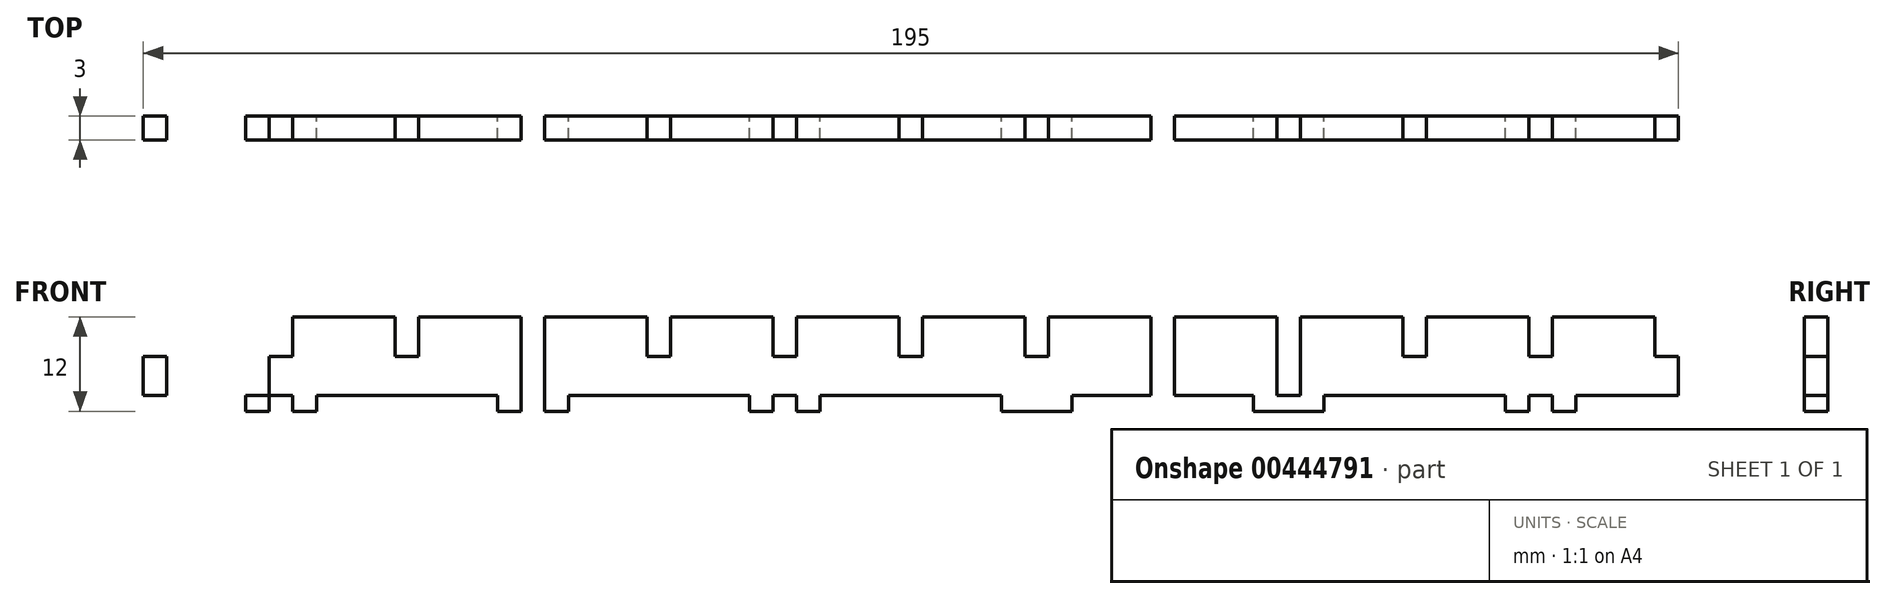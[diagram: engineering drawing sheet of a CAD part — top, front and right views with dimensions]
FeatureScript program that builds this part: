
annotation { "Feature Type Name" : "Feature", "Feature Type Description" : "" }
export const myFeature = defineFeature(function(context is Context, id is Id, definition is map)
    precondition{}
    {
        {
            var Q0;
            Q0=qCreatedBy(makeId("Front.planeOp"),FACE);
            var sketch = newSketch(context, id + "F0", { "sketchPlane" : qUnion([Q0])});
            skLineSegment(sketch, "E0", {"start": v(0, 0) * mm, "end": v(11.5, 0) * mm});
            skLineSegment(sketch, "E1", {"start": v(11.5, 0) * mm, "end": v(11.5, -2) * mm});
            skLineSegment(sketch, "E2", {"start": v(11.5, -2) * mm, "end": v(20.5, -2) * mm});
            skLineSegment(sketch, "E3", {"start": v(20.5, -2) * mm, "end": v(20.5, 0) * mm});
            skLineSegment(sketch, "E4", {"start": v(20.5, 0) * mm, "end": v(43.5, 0) * mm});
            skLineSegment(sketch, "E5", {"start": v(43.5, 0) * mm, "end": v(43.5, -2) * mm});
            skLineSegment(sketch, "E6", {"start": v(43.5, -2) * mm, "end": v(52.5, -2) * mm});
            skLineSegment(sketch, "E7", {"start": v(52.5, -2) * mm, "end": v(52.5, 0) * mm});
            skLineSegment(sketch, "E8", {"start": v(0, 0) * mm, "end": v(0, 10) * mm});
            skPoint(sketch, "E9.oppositeSnap0", {"position": v(0, 5) * mm});
            skLineSegment(sketch, "E9.bottom", {"start": v(0, 10) * mm, "end": v(-1.5, 10) * mm});
            skLineSegment(sketch, "E9.top", {"start": v(0, 5) * mm, "end": v(-1.5, 5) * mm});
            skLineSegment(sketch, "E9.left", {"start": v(0, 10) * mm, "end": v(0, 5) * mm});
            skLineSegment(sketch, "E9.right", {"start": v(-1.5, 10) * mm, "end": v(-1.5, 5) * mm});
            skLineSegment(sketch, "E10.bottom", {"start": v(14.5, 10) * mm, "end": v(17.5, 10) * mm});
            skLineSegment(sketch, "E10.top", {"start": v(14.5, 5) * mm, "end": v(17.5, 5) * mm});
            skLineSegment(sketch, "E10.left", {"start": v(14.5, 10) * mm, "end": v(14.5, 5) * mm});
            skLineSegment(sketch, "E10.right", {"start": v(17.5, 10) * mm, "end": v(17.5, 5) * mm});
            skLineSegment(sketch, "E11.top", {"start": v(0, 0) * mm, "end": v(-1.5, 0) * mm});
            skLineSegment(sketch, "E11.left", {"start": v(0, 5) * mm, "end": v(0, 0) * mm});
            skLineSegment(sketch, "E11.right", {"start": v(-1.5, 5) * mm, "end": v(-1.5, 0) * mm});
            skLineSegment(sketch, "E12.top", {"start": v(14.5, -2) * mm, "end": v(17.5, -2) * mm});
            skLineSegment(sketch, "E12.left", {"start": v(14.5, 5) * mm, "end": v(14.5, -2) * mm});
            skLineSegment(sketch, "E12.right", {"start": v(17.5, 5) * mm, "end": v(17.5, -2) * mm});
            skLineSegment(sketch, "E13.bottom", {"start": v(0, 10) * mm, "end": v(1.5, 10) * mm});
            skLineSegment(sketch, "E13.top", {"start": v(0, 5) * mm, "end": v(1.5, 5) * mm});
            skLineSegment(sketch, "E13.right", {"start": v(1.5, 10) * mm, "end": v(1.5, 5) * mm});
            skLineSegment(sketch, "E14.top", {"start": v(0, 0) * mm, "end": v(1.5, 0) * mm});
            skLineSegment(sketch, "E14.right", {"start": v(1.5, 5) * mm, "end": v(1.5, 0) * mm});
            skLineSegment(sketch, "E15.bottom", {"start": v(11.5, 10) * mm, "end": v(20.5, 10) * mm});
            skLineSegment(sketch, "E15.top", {"start": v(11.5, 13) * mm, "end": v(20.5, 13) * mm});
            skLineSegment(sketch, "E15.left", {"start": v(11.5, 10) * mm, "end": v(11.5, 13) * mm});
            skLineSegment(sketch, "E15.right", {"start": v(20.5, 10) * mm, "end": v(20.5, 13) * mm});
            skLineSegment(sketch, "E16", {"start": v(52.5, 0) * mm, "end": v(75.5, 0) * mm});
            skLineSegment(sketch, "E17", {"start": v(75.5, 0) * mm, "end": v(75.5, -2) * mm});
            skLineSegment(sketch, "E18", {"start": v(75.5, -2) * mm, "end": v(84.5, -2) * mm});
            skLineSegment(sketch, "E19", {"start": v(84.5, -2) * mm, "end": v(84.5, 0) * mm});
            skLineSegment(sketch, "E20", {"start": v(84.5, 0) * mm, "end": v(96, 0) * mm});
            skLineSegment(sketch, "E21", {"start": v(96, 0) * mm, "end": v(96, 19.13) * mm, "construction": true});
            skLineSegment(sketch, "E22", {"start": v(16, 10) * mm, "end": v(16, 11.65) * mm, "construction": true});
            skLineSegment(sketch, "E23.bottom", {"start": v(30.5, 0) * mm, "end": v(33.5, 0) * mm});
            skLineSegment(sketch, "E23.top", {"start": v(30.5, 5) * mm, "end": v(33.5, 5) * mm});
            skLineSegment(sketch, "E23.left", {"start": v(30.5, 0) * mm, "end": v(30.5, 5) * mm});
            skLineSegment(sketch, "E23.right", {"start": v(33.5, 0) * mm, "end": v(33.5, 5) * mm});
            skLineSegment(sketch, "E24.bottom", {"start": v(33.5, 5) * mm, "end": v(30.5, 5) * mm});
            skLineSegment(sketch, "E24.top", {"start": v(33.5, 10) * mm, "end": v(30.5, 10) * mm});
            skLineSegment(sketch, "E24.left", {"start": v(33.5, 5) * mm, "end": v(33.5, 10) * mm});
            skLineSegment(sketch, "E24.right", {"start": v(30.5, 5) * mm, "end": v(30.5, 10) * mm});
            skLineSegment(sketch, "E25", {"start": v(32, 0) * mm, "end": v(32, 2.31) * mm, "construction": true});
            skLineSegment(sketch, "E26.bottom", {"start": v(46.5, -2) * mm, "end": v(49.5, -2) * mm});
            skLineSegment(sketch, "E26.top", {"start": v(46.5, 5) * mm, "end": v(49.5, 5) * mm});
            skLineSegment(sketch, "E26.left", {"start": v(46.5, -2) * mm, "end": v(46.5, 5) * mm});
            skLineSegment(sketch, "E26.right", {"start": v(49.5, -2) * mm, "end": v(49.5, 5) * mm});
            skLineSegment(sketch, "E27.bottom", {"start": v(49.5, 5) * mm, "end": v(46.5, 5) * mm});
            skLineSegment(sketch, "E27.top", {"start": v(49.5, 10) * mm, "end": v(46.5, 10) * mm});
            skLineSegment(sketch, "E27.left", {"start": v(49.5, 5) * mm, "end": v(49.5, 10) * mm});
            skLineSegment(sketch, "E27.right", {"start": v(46.5, 5) * mm, "end": v(46.5, 10) * mm});
            skLineSegment(sketch, "E28.bottom", {"start": v(62.5, 0) * mm, "end": v(65.5, 0) * mm});
            skLineSegment(sketch, "E28.top", {"start": v(62.5, 5) * mm, "end": v(65.5, 5) * mm});
            skLineSegment(sketch, "E28.left", {"start": v(62.5, 0) * mm, "end": v(62.5, 5) * mm});
            skLineSegment(sketch, "E28.right", {"start": v(65.5, 0) * mm, "end": v(65.5, 5) * mm});
            skLineSegment(sketch, "E29.bottom", {"start": v(65.5, 5) * mm, "end": v(62.5, 5) * mm});
            skLineSegment(sketch, "E29.top", {"start": v(65.5, 10) * mm, "end": v(62.5, 10) * mm});
            skLineSegment(sketch, "E29.left", {"start": v(65.5, 5) * mm, "end": v(65.5, 10) * mm});
            skLineSegment(sketch, "E29.right", {"start": v(62.5, 5) * mm, "end": v(62.5, 10) * mm});
            skLineSegment(sketch, "E30.bottom", {"start": v(81.5, -2) * mm, "end": v(78.5, -2) * mm});
            skLineSegment(sketch, "E30.top", {"start": v(81.5, 5) * mm, "end": v(78.5, 5) * mm});
            skLineSegment(sketch, "E30.left", {"start": v(81.5, -2) * mm, "end": v(81.5, 5) * mm});
            skLineSegment(sketch, "E30.right", {"start": v(78.5, -2) * mm, "end": v(78.5, 5) * mm});
            skLineSegment(sketch, "E31.top", {"start": v(81.5, 10) * mm, "end": v(78.5, 10) * mm});
            skLineSegment(sketch, "E31.left", {"start": v(81.5, 5) * mm, "end": v(81.5, 10) * mm});
            skLineSegment(sketch, "E31.right", {"start": v(78.5, 5) * mm, "end": v(78.5, 10) * mm});
            skLineSegment(sketch, "E32.bottom", {"start": v(96, 0) * mm, "end": v(94.5, 0) * mm});
            skLineSegment(sketch, "E32.top", {"start": v(96, 5) * mm, "end": v(94.5, 5) * mm});
            skLineSegment(sketch, "E32.left", {"start": v(96, 0) * mm, "end": v(96, 5) * mm});
            skLineSegment(sketch, "E32.right", {"start": v(94.5, 0) * mm, "end": v(94.5, 5) * mm});
            skLineSegment(sketch, "E33.left", {"start": v(96, 5) * mm, "end": v(96, 5) * mm});
            skLineSegment(sketch, "E33.right", {"start": v(94.5, 5) * mm, "end": v(94.5, 5) * mm});
            skLineSegment(sketch, "E34.top", {"start": v(96, 10) * mm, "end": v(94.5, 10) * mm});
            skLineSegment(sketch, "E34.left", {"start": v(96, 5) * mm, "end": v(96, 10) * mm});
            skLineSegment(sketch, "E34.right", {"start": v(94.5, 5) * mm, "end": v(94.5, 10) * mm});
            skLineSegment(sketch, "E35", {"start": v(48, -2) * mm, "end": v(48, 0) * mm, "construction": true});
            skLineSegment(sketch, "E36", {"start": v(64, 0) * mm, "end": v(64, 2.67) * mm, "construction": true});
            skLineSegment(sketch, "E37", {"start": v(80, -2) * mm, "end": v(80, 0) * mm, "construction": true});
            skLineSegment(sketch, "E38", {"start": v(1.5, 10) * mm, "end": v(96, 10) * mm});
            skLineSegment(sketch, "E39.MirrorCS", {"start": v(96, 5) * mm, "end": v(97.5, 5) * mm});
            skLineSegment(sketch, "E40.MirrorCS", {"start": v(145.5, 5) * mm, "end": v(142.5, 5) * mm});
            skLineSegment(sketch, "E41.MirrorCS", {"start": v(110.5, 5) * mm, "end": v(113.5, 5) * mm});
            skLineSegment(sketch, "E42.MirrorCS", {"start": v(129.5, 5) * mm, "end": v(126.5, 5) * mm});
            skLineSegment(sketch, "E43.MirrorCS", {"start": v(177.5, 5) * mm, "end": v(174.5, 5) * mm});
            skLineSegment(sketch, "E44.MirrorCS", {"start": v(192, 5) * mm, "end": v(190.5, 5) * mm});
            skLineSegment(sketch, "E45.MirrorCS", {"start": v(192, 5) * mm, "end": v(193.5, 5) * mm});
            skLineSegment(sketch, "E46.MirrorCS", {"start": v(142.5, 5) * mm, "end": v(145.5, 5) * mm});
            skLineSegment(sketch, "E47.MirrorCS", {"start": v(126.5, 5) * mm, "end": v(129.5, 5) * mm});
            skLineSegment(sketch, "E48.MirrorCS", {"start": v(192, 10) * mm, "end": v(190.5, 10) * mm});
            skLineSegment(sketch, "E49.MirrorCS", {"start": v(171.5, -2) * mm, "end": v(171.5, 0) * mm});
            skLineSegment(sketch, "E50.MirrorCS", {"start": v(180.5, 0) * mm, "end": v(180.5, -2) * mm});
            skLineSegment(sketch, "E51.MirrorCS", {"start": v(177.5, 10) * mm, "end": v(174.5, 10) * mm});
            skLineSegment(sketch, "E52.MirrorCS", {"start": v(116.5, 0) * mm, "end": v(116.5, -2) * mm});
            skLineSegment(sketch, "E53.MirrorCS", {"start": v(177.5, -2) * mm, "end": v(174.5, -2) * mm});
            skLineSegment(sketch, "E54.MirrorCS", {"start": v(192, 0) * mm, "end": v(190.5, 0) * mm});
            skLineSegment(sketch, "E55.MirrorCS", {"start": v(126.5, 10) * mm, "end": v(129.5, 10) * mm});
            skLineSegment(sketch, "E56.MirrorCS", {"start": v(145.5, -2) * mm, "end": v(142.5, -2) * mm});
            skLineSegment(sketch, "E57.MirrorCS", {"start": v(110.5, -2) * mm, "end": v(113.5, -2) * mm});
            skLineSegment(sketch, "E58.MirrorCS", {"start": v(192, 0) * mm, "end": v(193.5, 0) * mm});
            skLineSegment(sketch, "E59.MirrorCS", {"start": v(96, 10) * mm, "end": v(97.5, 10) * mm});
            skLineSegment(sketch, "E60.MirrorCS", {"start": v(110.5, 10) * mm, "end": v(113.5, 10) * mm});
            skLineSegment(sketch, "E61.MirrorCS", {"start": v(142.5, 10) * mm, "end": v(145.5, 10) * mm});
            skLineSegment(sketch, "E62.MirrorCS", {"start": v(107.5, -2) * mm, "end": v(107.5, 0) * mm});
            skLineSegment(sketch, "E63.MirrorCS", {"start": v(192, 10) * mm, "end": v(193.5, 10) * mm});
            skLineSegment(sketch, "E64.MirrorCS", {"start": v(96, 0) * mm, "end": v(97.5, 0) * mm});
            skLineSegment(sketch, "E65.MirrorCS", {"start": v(139.5, -2) * mm, "end": v(139.5, 0) * mm});
            skLineSegment(sketch, "E66.MirrorCS", {"start": v(129.5, 0) * mm, "end": v(126.5, 0) * mm});
            skLineSegment(sketch, "E67.MirrorCS", {"start": v(148.5, 0) * mm, "end": v(148.5, -2) * mm});
            skLineSegment(sketch, "E68.MirrorCS", {"start": v(192, 5) * mm, "end": v(192, 0) * mm});
            skLineSegment(sketch, "E69.MirrorCS", {"start": v(112, -2) * mm, "end": v(112, 0) * mm, "construction": true});
            skLineSegment(sketch, "E70.MirrorCS", {"start": v(176, 10) * mm, "end": v(176, 11.65) * mm, "construction": true});
            skLineSegment(sketch, "E71.MirrorCS", {"start": v(192, 10) * mm, "end": v(192, 5) * mm});
            skLineSegment(sketch, "E72.MirrorCS", {"start": v(161.5, 0) * mm, "end": v(158.5, 0) * mm});
            skLineSegment(sketch, "E73.MirrorCS", {"start": v(128, 0) * mm, "end": v(128, 2.67) * mm, "construction": true});
            skLineSegment(sketch, "E74.MirrorCS", {"start": v(160, 0) * mm, "end": v(160, 2.31) * mm, "construction": true});
            skLineSegment(sketch, "E75.MirrorCS", {"start": v(144, -2) * mm, "end": v(144, 0) * mm, "construction": true});
            skLineSegment(sketch, "E76.MirrorCS", {"start": v(161.5, 5) * mm, "end": v(158.5, 5) * mm});
            skLineSegment(sketch, "E77.MirrorCS", {"start": v(171.5, 0) * mm, "end": v(148.5, 0) * mm});
            skLineSegment(sketch, "E78.MirrorCS", {"start": v(180.5, -2) * mm, "end": v(171.5, -2) * mm});
            skLineSegment(sketch, "E79.MirrorCS", {"start": v(192, 0) * mm, "end": v(180.5, 0) * mm});
            skLineSegment(sketch, "E80.MirrorCS", {"start": v(177.5, 10) * mm, "end": v(177.5, 5) * mm});
            skLineSegment(sketch, "E81.MirrorCS", {"start": v(158.5, 0) * mm, "end": v(158.5, 5) * mm});
            skLineSegment(sketch, "E82.MirrorCS", {"start": v(129.5, 0) * mm, "end": v(129.5, 5) * mm});
            skLineSegment(sketch, "E83.MirrorCS", {"start": v(97.5, 5) * mm, "end": v(97.5, 10) * mm});
            skPoint(sketch, "E84.MirrorP", {"position": v(192, 5) * mm});
            skLineSegment(sketch, "E85.MirrorCS", {"start": v(139.5, 0) * mm, "end": v(116.5, 0) * mm});
            skLineSegment(sketch, "E86.MirrorCS", {"start": v(126.5, 5) * mm, "end": v(126.5, 10) * mm});
            skLineSegment(sketch, "E87.MirrorCS", {"start": v(161.5, 5) * mm, "end": v(161.5, 10) * mm});
            skLineSegment(sketch, "E88.MirrorCS", {"start": v(180.5, 10) * mm, "end": v(180.5, 13) * mm});
            skLineSegment(sketch, "E89.MirrorCS", {"start": v(180.5, 13) * mm, "end": v(171.5, 13) * mm});
            skLineSegment(sketch, "E90.MirrorCS", {"start": v(158.5, 5) * mm, "end": v(158.5, 10) * mm});
            skLineSegment(sketch, "E91.MirrorCS", {"start": v(161.5, 0) * mm, "end": v(161.5, 5) * mm});
            skLineSegment(sketch, "E92.MirrorCS", {"start": v(107.5, 0) * mm, "end": v(96, 0) * mm});
            skLineSegment(sketch, "E93.MirrorCS", {"start": v(142.5, 5) * mm, "end": v(142.5, 10) * mm});
            skLineSegment(sketch, "E94.MirrorCS", {"start": v(193.5, 5) * mm, "end": v(193.5, 0) * mm});
            skLineSegment(sketch, "E95.MirrorCS", {"start": v(110.5, 5) * mm, "end": v(110.5, 10) * mm});
            skLineSegment(sketch, "E96.MirrorCS", {"start": v(180.5, 10) * mm, "end": v(171.5, 10) * mm});
            skLineSegment(sketch, "E97.MirrorCS", {"start": v(158.5, 10) * mm, "end": v(161.5, 10) * mm});
            skLineSegment(sketch, "E98.MirrorCS", {"start": v(145.5, 5) * mm, "end": v(145.5, 10) * mm});
            skLineSegment(sketch, "E99.MirrorCS", {"start": v(113.5, -2) * mm, "end": v(113.5, 5) * mm});
            skLineSegment(sketch, "E100.MirrorCS", {"start": v(174.5, 5) * mm, "end": v(174.5, -2) * mm});
            skLineSegment(sketch, "E101.MirrorCS", {"start": v(142.5, -2) * mm, "end": v(142.5, 5) * mm});
            skLineSegment(sketch, "E102.MirrorCS", {"start": v(113.5, 5) * mm, "end": v(113.5, 10) * mm});
            skLineSegment(sketch, "E103.MirrorCS", {"start": v(190.5, 10) * mm, "end": v(96, 10) * mm});
            skLineSegment(sketch, "E104.MirrorCS", {"start": v(190.5, 5) * mm, "end": v(190.5, 0) * mm});
            skLineSegment(sketch, "E105.MirrorCS", {"start": v(158.5, 5) * mm, "end": v(161.5, 5) * mm});
            skLineSegment(sketch, "E106.MirrorCS", {"start": v(126.5, 0) * mm, "end": v(126.5, 5) * mm});
            skLineSegment(sketch, "E107.MirrorCS", {"start": v(97.5, 0) * mm, "end": v(97.5, 5) * mm});
            skLineSegment(sketch, "E108.MirrorCS", {"start": v(174.5, 10) * mm, "end": v(174.5, 5) * mm});
            skLineSegment(sketch, "E109.MirrorCS", {"start": v(110.5, -2) * mm, "end": v(110.5, 5) * mm});
            skLineSegment(sketch, "E110.MirrorCS", {"start": v(177.5, 5) * mm, "end": v(177.5, -2) * mm});
            skLineSegment(sketch, "E111.MirrorCS", {"start": v(116.5, -2) * mm, "end": v(107.5, -2) * mm});
            skLineSegment(sketch, "E112.MirrorCS", {"start": v(145.5, -2) * mm, "end": v(145.5, 5) * mm});
            skLineSegment(sketch, "E113.MirrorCS", {"start": v(193.5, 10) * mm, "end": v(193.5, 5) * mm});
            skLineSegment(sketch, "E114.MirrorCS", {"start": v(129.5, 5) * mm, "end": v(129.5, 10) * mm});
            skLineSegment(sketch, "E115.MirrorCS", {"start": v(192, 0) * mm, "end": v(192, 10) * mm});
            skLineSegment(sketch, "E116.MirrorCS", {"start": v(148.5, -2) * mm, "end": v(139.5, -2) * mm});
            skLineSegment(sketch, "E117.MirrorCS", {"start": v(171.5, 10) * mm, "end": v(171.5, 13) * mm});
            skLineSegment(sketch, "E118.MirrorCS", {"start": v(190.5, 10) * mm, "end": v(190.5, 5) * mm});
            skLineSegment(sketch, "E119.top", {"start": v(14.5, 13) * mm, "end": v(17.5, 13) * mm});
            skLineSegment(sketch, "E119.left", {"start": v(14.5, 10) * mm, "end": v(14.5, 13) * mm});
            skLineSegment(sketch, "E119.right", {"start": v(17.5, 10) * mm, "end": v(17.5, 13) * mm});
            skLineSegment(sketch, "E120.bottom", {"start": v(174.5, 10) * mm, "end": v(177.5, 10) * mm});
            skLineSegment(sketch, "E120.top", {"start": v(174.5, 13) * mm, "end": v(177.5, 13) * mm});
            skLineSegment(sketch, "E120.left", {"start": v(174.5, 10) * mm, "end": v(174.5, 13) * mm});
            skLineSegment(sketch, "E120.right", {"start": v(177.5, 10) * mm, "end": v(177.5, 13) * mm});
            skLineSegment(sketch, "E121", {"start": v(11.5, 0) * mm, "end": v(180.5, 0) * mm});
            skSolve(sketch);
        }
        {
            var Q0;
            {var subQ5=sQuery(id+"F0.wireOp",EDGE,"E0");Q0=makeQuery(id+"F0.imprint","IMPRINT",FACE,{"disambiguationData":[TD([[makeQuery(id+"F0.imprint","IMPRINT",EDGE,{"derivedFrom":subQ5}),1.0]])]});}
            var Q1;
            {var subQ2=sQuery(id+"F0.wireOp",EDGE,"E10.right");Q1=makeQuery(id+"F0.imprint","IMPRINT",FACE,{"disambiguationData":[TD([[makeQuery(id+"F0.imprint","IMPRINT",EDGE,{"derivedFrom":subQ2}),1.0]])]});}
            var Q2;
            {var subQ0=sQuery(id+"F0.wireOp",EDGE,"E5");Q2=makeQuery(id+"F0.imprint","IMPRINT",FACE,{"disambiguationData":[TD([[makeQuery(id+"F0.imprint","IMPRINT",EDGE,{"derivedFrom":subQ0}),1.0]])]});}
            var Q3;
            {var subQ0=sQuery(id+"F0.wireOp",EDGE,"E7");Q3=makeQuery(id+"F0.imprint","IMPRINT",FACE,{"disambiguationData":[TD([[makeQuery(id+"F0.imprint","IMPRINT",EDGE,{"derivedFrom":subQ0}),1.0]])]});}
            var Q4;
            {var subQ0=sQuery(id+"F0.wireOp",EDGE,"E17");Q4=makeQuery(id+"F0.imprint","IMPRINT",FACE,{"disambiguationData":[TD([[makeQuery(id+"F0.imprint","IMPRINT",EDGE,{"derivedFrom":subQ0}),1.0]])]});}
            var Q5;
            {var subQ0=sQuery(id+"F0.wireOp",EDGE,"E19");Q5=makeQuery(id+"F0.imprint","IMPRINT",FACE,{"disambiguationData":[TD([[makeQuery(id+"F0.imprint","IMPRINT",EDGE,{"derivedFrom":subQ0}),1.0]])]});}
            var Q6;
            {var subQ0=sQuery(id+"F0.wireOp",EDGE,"E62.MirrorCS");Q6=makeQuery(id+"F0.imprint","IMPRINT",FACE,{"disambiguationData":[TD([[makeQuery(id+"F0.imprint","IMPRINT",EDGE,{"derivedFrom":subQ0}),-1.0]])]});}
            var Q7;
            {var subQ0=sQuery(id+"F0.wireOp",EDGE,"E52.MirrorCS");Q7=makeQuery(id+"F0.imprint","IMPRINT",FACE,{"disambiguationData":[TD([[makeQuery(id+"F0.imprint","IMPRINT",EDGE,{"derivedFrom":subQ0}),-1.0]])]});}
            var Q8;
            {var subQ0=sQuery(id+"F0.wireOp",EDGE,"E65.MirrorCS");Q8=makeQuery(id+"F0.imprint","IMPRINT",FACE,{"disambiguationData":[TD([[makeQuery(id+"F0.imprint","IMPRINT",EDGE,{"derivedFrom":subQ0}),-1.0]])]});}
            var Q9;
            {var subQ0=sQuery(id+"F0.wireOp",EDGE,"E67.MirrorCS");Q9=makeQuery(id+"F0.imprint","IMPRINT",FACE,{"disambiguationData":[TD([[makeQuery(id+"F0.imprint","IMPRINT",EDGE,{"derivedFrom":subQ0}),-1.0]])]});}
            var Q10;
            {var subQ0=sQuery(id+"F0.wireOp",EDGE,"E49.MirrorCS");Q10=makeQuery(id+"F0.imprint","IMPRINT",FACE,{"disambiguationData":[TD([[makeQuery(id+"F0.imprint","IMPRINT",EDGE,{"derivedFrom":subQ0}),-1.0]])]});}
            var Q11;
            {var subQ0=sQuery(id+"F0.wireOp",EDGE,"E50.MirrorCS");Q11=makeQuery(id+"F0.imprint","IMPRINT",FACE,{"disambiguationData":[TD([[makeQuery(id+"F0.imprint","IMPRINT",EDGE,{"derivedFrom":subQ0}),-1.0]])]});}
            var Q12;
            {var subQ1=sQuery(id+"F0.wireOp",EDGE,"E23.right");Q12=makeQuery(id+"F0.imprint","IMPRINT",FACE,{"disambiguationData":[TD([[makeQuery(id+"F0.imprint","IMPRINT",EDGE,{"derivedFrom":subQ1}),-1.0]])]});}
            var Q13;
            {var subQ2=sQuery(id+"F0.wireOp",EDGE,"E27.left");Q13=makeQuery(id+"F0.imprint","IMPRINT",FACE,{"disambiguationData":[TD([[makeQuery(id+"F0.imprint","IMPRINT",EDGE,{"derivedFrom":subQ2}),-1.0]])]});}
            var Q14;
            {var subQ1=sQuery(id+"F0.wireOp",EDGE,"E28.right");Q14=makeQuery(id+"F0.imprint","IMPRINT",FACE,{"disambiguationData":[TD([[makeQuery(id+"F0.imprint","IMPRINT",EDGE,{"derivedFrom":subQ1}),-1.0]])]});}
            var Q15;
            {var subQ2=sQuery(id+"F0.wireOp",EDGE,"E31.left");Q15=makeQuery(id+"F0.imprint","IMPRINT",FACE,{"disambiguationData":[TD([[makeQuery(id+"F0.imprint","IMPRINT",EDGE,{"derivedFrom":subQ2}),-1.0]])]});}
            var Q16;
            {var subQ2=sQuery(id+"F0.wireOp",EDGE,"E83.MirrorCS");Q16=makeQuery(id+"F0.imprint","IMPRINT",FACE,{"disambiguationData":[TD([[makeQuery(id+"F0.imprint","IMPRINT",EDGE,{"derivedFrom":subQ2}),-1.0]])]});}
            var Q17;
            {var subQ1=sQuery(id+"F0.wireOp",EDGE,"E86.MirrorCS");Q17=makeQuery(id+"F0.imprint","IMPRINT",FACE,{"disambiguationData":[TD([[makeQuery(id+"F0.imprint","IMPRINT",EDGE,{"derivedFrom":subQ1}),1.0]])]});}
            var Q18;
            {var subQ6=sQuery(id+"F0.wireOp",EDGE,"E82.MirrorCS");Q18=makeQuery(id+"F0.imprint","IMPRINT",FACE,{"disambiguationData":[TD([[makeQuery(id+"F0.imprint","IMPRINT",EDGE,{"derivedFrom":subQ6}),-1.0]])]});}
            var Q19;
            {var subQ7=sQuery(id+"F0.wireOp",EDGE,"E81.MirrorCS");Q19=makeQuery(id+"F0.imprint","IMPRINT",FACE,{"disambiguationData":[TD([[makeQuery(id+"F0.imprint","IMPRINT",EDGE,{"derivedFrom":subQ7}),1.0]])]});}
            var Q20;
            {var subQ7=sQuery(id+"F0.wireOp",EDGE,"E87.MirrorCS");Q20=makeQuery(id+"F0.imprint","IMPRINT",FACE,{"disambiguationData":[TD([[makeQuery(id+"F0.imprint","IMPRINT",EDGE,{"derivedFrom":subQ7}),-1.0]])]});}
            var Q21;
            {var subQ1=sQuery(id+"F0.wireOp",EDGE,"E80.MirrorCS");Q21=makeQuery(id+"F0.imprint","IMPRINT",FACE,{"disambiguationData":[TD([[makeQuery(id+"F0.imprint","IMPRINT",EDGE,{"derivedFrom":subQ1}),1.0]])]});}
            var Q22;
            Q22=makeQuery(id+"F0.imprint","IMPRINT",FACE,{"disambiguationData":[TD([[makeQuery(id+"F0.imprint","IMPRINT",EDGE,{"derivedFrom":sQuery(id+"F0.wireOp",EDGE,"E13.top")}),-1.0]])]});
            var Q23;
            Q23=makeQuery(id+"F0.imprint","IMPRINT",FACE,{"disambiguationData":[TD([[makeQuery(id+"F0.imprint","IMPRINT",EDGE,{"derivedFrom":sQuery(id+"F0.wireOp",EDGE,"E9.top")}),1.0]])]});
            var Q24;
            {var subQ0=sQuery(id+"F0.wireOp",EDGE,"E12.top");Q24=makeQuery(id+"F0.imprint","IMPRINT",FACE,{"disambiguationData":[TD([[makeQuery(id+"F0.imprint","IMPRINT",EDGE,{"derivedFrom":subQ0}),1.0]])]});}
            var Q25;
            {var subQ0=sQuery(id+"F0.wireOp",EDGE,"E10.top");Q25=makeQuery(id+"F0.imprint","IMPRINT",FACE,{"disambiguationData":[TD([[makeQuery(id+"F0.imprint","IMPRINT",EDGE,{"derivedFrom":subQ0}),-1.0]])]});}
            var Q26;
            {var subQ0=sQuery(id+"F0.wireOp",EDGE,"E23.left");Q26=makeQuery(id+"F0.imprint","IMPRINT",FACE,{"disambiguationData":[TD([[makeQuery(id+"F0.imprint","IMPRINT",EDGE,{"derivedFrom":subQ0}),-1.0]])]});}
            var Q27;
            {var subQ0=sQuery(id+"F0.wireOp",EDGE,"E26.bottom");Q27=makeQuery(id+"F0.imprint","IMPRINT",FACE,{"disambiguationData":[TD([[makeQuery(id+"F0.imprint","IMPRINT",EDGE,{"derivedFrom":subQ0}),1.0]])]});}
            var Q28;
            {var subQ0=sQuery(id+"F0.wireOp",EDGE,"E27.bottom");Q28=makeQuery(id+"F0.imprint","IMPRINT",FACE,{"disambiguationData":[TD([[makeQuery(id+"F0.imprint","IMPRINT",EDGE,{"derivedFrom":subQ0}),1.0]])]});}
            var Q29;
            {var subQ0=sQuery(id+"F0.wireOp",EDGE,"E1");Q29=makeQuery(id+"F0.imprint","IMPRINT",FACE,{"disambiguationData":[TD([[makeQuery(id+"F0.imprint","IMPRINT",EDGE,{"derivedFrom":subQ0}),1.0]])]});}
            var Q30;
            {var subQ0=sQuery(id+"F0.wireOp",EDGE,"E3");Q30=makeQuery(id+"F0.imprint","IMPRINT",FACE,{"disambiguationData":[TD([[makeQuery(id+"F0.imprint","IMPRINT",EDGE,{"derivedFrom":subQ0}),1.0]])]});}
            var Q31;
            {var subQ0=sQuery(id+"F0.wireOp",EDGE,"E28.left");Q31=makeQuery(id+"F0.imprint","IMPRINT",FACE,{"disambiguationData":[TD([[makeQuery(id+"F0.imprint","IMPRINT",EDGE,{"derivedFrom":subQ0}),-1.0]])]});}
            var Q32;
            {var subQ0=sQuery(id+"F0.wireOp",EDGE,"E30.top");Q32=makeQuery(id+"F0.imprint","IMPRINT",FACE,{"disambiguationData":[TD([[makeQuery(id+"F0.imprint","IMPRINT",EDGE,{"derivedFrom":subQ0}),1.0]])]});}
            var Q33;
            {var subQ0=sQuery(id+"F0.wireOp",EDGE,"E30.bottom");Q33=makeQuery(id+"F0.imprint","IMPRINT",FACE,{"disambiguationData":[TD([[makeQuery(id+"F0.imprint","IMPRINT",EDGE,{"derivedFrom":subQ0}),-1.0]])]});}
            var Q34;
            Q34=makeQuery(id+"F0.imprint","IMPRINT",FACE,{"disambiguationData":[TD([[makeQuery(id+"F0.imprint","IMPRINT",EDGE,{"derivedFrom":sQuery(id+"F0.wireOp",EDGE,"E39.MirrorCS")}),-1.0]])]});
            var Q35;
            {var subQ0=sQuery(id+"F0.wireOp",EDGE,"E41.MirrorCS");Q35=makeQuery(id+"F0.imprint","IMPRINT",FACE,{"disambiguationData":[TD([[makeQuery(id+"F0.imprint","IMPRINT",EDGE,{"derivedFrom":subQ0}),-1.0]])]});}
            var Q36;
            {var subQ0=sQuery(id+"F0.wireOp",EDGE,"E111.MirrorCS");var subQ1=sQuery(id+"F0.wireOp",EDGE,"E99.MirrorCS");var subQ2=makeQuery(id+"F0.imprint","INTERSECT",VERTEX,{"derivedFrom":[subQ1,subQ0]});Q36=makeQuery(id+"F0.imprint","IMPRINT",FACE,{"disambiguationData":[TD([[makeQuery(id+"F0.imprint","IMPRINT",EDGE,{"disambiguationData":[TD([[subQ2,-1.0]])],"derivedFrom":subQ1}),1.0]])]});}
            var Q37;
            Q37=makeQuery(id+"F0.imprint","IMPRINT",FACE,{"disambiguationData":[TD([[makeQuery(id+"F0.imprint","IMPRINT",EDGE,{"derivedFrom":sQuery(id+"F0.wireOp",EDGE,"E47.MirrorCS")}),-1.0]])]});
            var Q38;
            {var subQ0=sQuery(id+"F0.wireOp",EDGE,"E46.MirrorCS");Q38=makeQuery(id+"F0.imprint","IMPRINT",FACE,{"disambiguationData":[TD([[makeQuery(id+"F0.imprint","IMPRINT",EDGE,{"derivedFrom":subQ0}),-1.0]])]});}
            var Q39;
            {var subQ0=sQuery(id+"F0.wireOp",EDGE,"E116.MirrorCS");var subQ1=sQuery(id+"F0.wireOp",EDGE,"E101.MirrorCS");var subQ2=makeQuery(id+"F0.imprint","INTERSECT",VERTEX,{"derivedFrom":[subQ1,subQ0]});Q39=makeQuery(id+"F0.imprint","IMPRINT",FACE,{"disambiguationData":[TD([[makeQuery(id+"F0.imprint","IMPRINT",EDGE,{"disambiguationData":[TD([[subQ2,-1.0]])],"derivedFrom":subQ1}),-1.0]])]});}
            var Q40;
            {var subQ0=sQuery(id+"F0.wireOp",EDGE,"E81.MirrorCS");Q40=makeQuery(id+"F0.imprint","IMPRINT",FACE,{"disambiguationData":[TD([[makeQuery(id+"F0.imprint","IMPRINT",EDGE,{"derivedFrom":subQ0}),-1.0]])]});}
            var Q41;
            {var subQ0=sQuery(id+"F0.wireOp",EDGE,"E32.right");Q41=makeQuery(id+"F0.imprint","IMPRINT",FACE,{"disambiguationData":[TD([[makeQuery(id+"F0.imprint","IMPRINT",EDGE,{"derivedFrom":subQ0}),-1.0]])]});}
            var Q42;
            {var subQ0=sQuery(id+"F0.wireOp",EDGE,"E43.MirrorCS");Q42=makeQuery(id+"F0.imprint","IMPRINT",FACE,{"disambiguationData":[TD([[makeQuery(id+"F0.imprint","IMPRINT",EDGE,{"derivedFrom":subQ0}),1.0]])]});}
            var Q43;
            {var subQ0=sQuery(id+"F0.wireOp",EDGE,"E100.MirrorCS");var subQ1=sQuery(id+"F0.wireOp",EDGE,"E78.MirrorCS");var subQ2=makeQuery(id+"F0.imprint","INTERSECT",VERTEX,{"derivedFrom":[subQ1,subQ0]});Q43=makeQuery(id+"F0.imprint","IMPRINT",FACE,{"disambiguationData":[TD([[makeQuery(id+"F0.imprint","IMPRINT",EDGE,{"disambiguationData":[TD([[subQ2,1.0]])],"derivedFrom":subQ1}),-1.0]])]});}
            var Q44;
            {var subQ0=sQuery(id+"F0.wireOp",EDGE,"E44.MirrorCS");Q44=makeQuery(id+"F0.imprint","IMPRINT",FACE,{"disambiguationData":[TD([[makeQuery(id+"F0.imprint","IMPRINT",EDGE,{"derivedFrom":subQ0}),1.0]])]});}
            var Q45;
            {var subQ0=sQuery(id+"F0.wireOp",EDGE,"E45.MirrorCS");Q45=makeQuery(id+"F0.imprint","IMPRINT",FACE,{"disambiguationData":[TD([[makeQuery(id+"F0.imprint","IMPRINT",EDGE,{"derivedFrom":subQ0}),-1.0]])]});}
            extrude(context, id + "F1", {"entities" : qUnion([Q0, Q1, Q2, Q3, Q4, Q5, Q6, Q7, Q8, Q9, Q10, Q11, Q12, Q13, Q14, Q15, Q16, Q17, Q18, Q19, Q20, Q21, Q22, Q23, Q24, Q25, Q26, Q27, Q28, Q29, Q30, Q31, Q32, Q33, Q34, Q35, Q36, Q37, Q38, Q39, Q40, Q41, Q42, Q43, Q44, Q45]), "depth" : 3 * mm});
        }
    });
